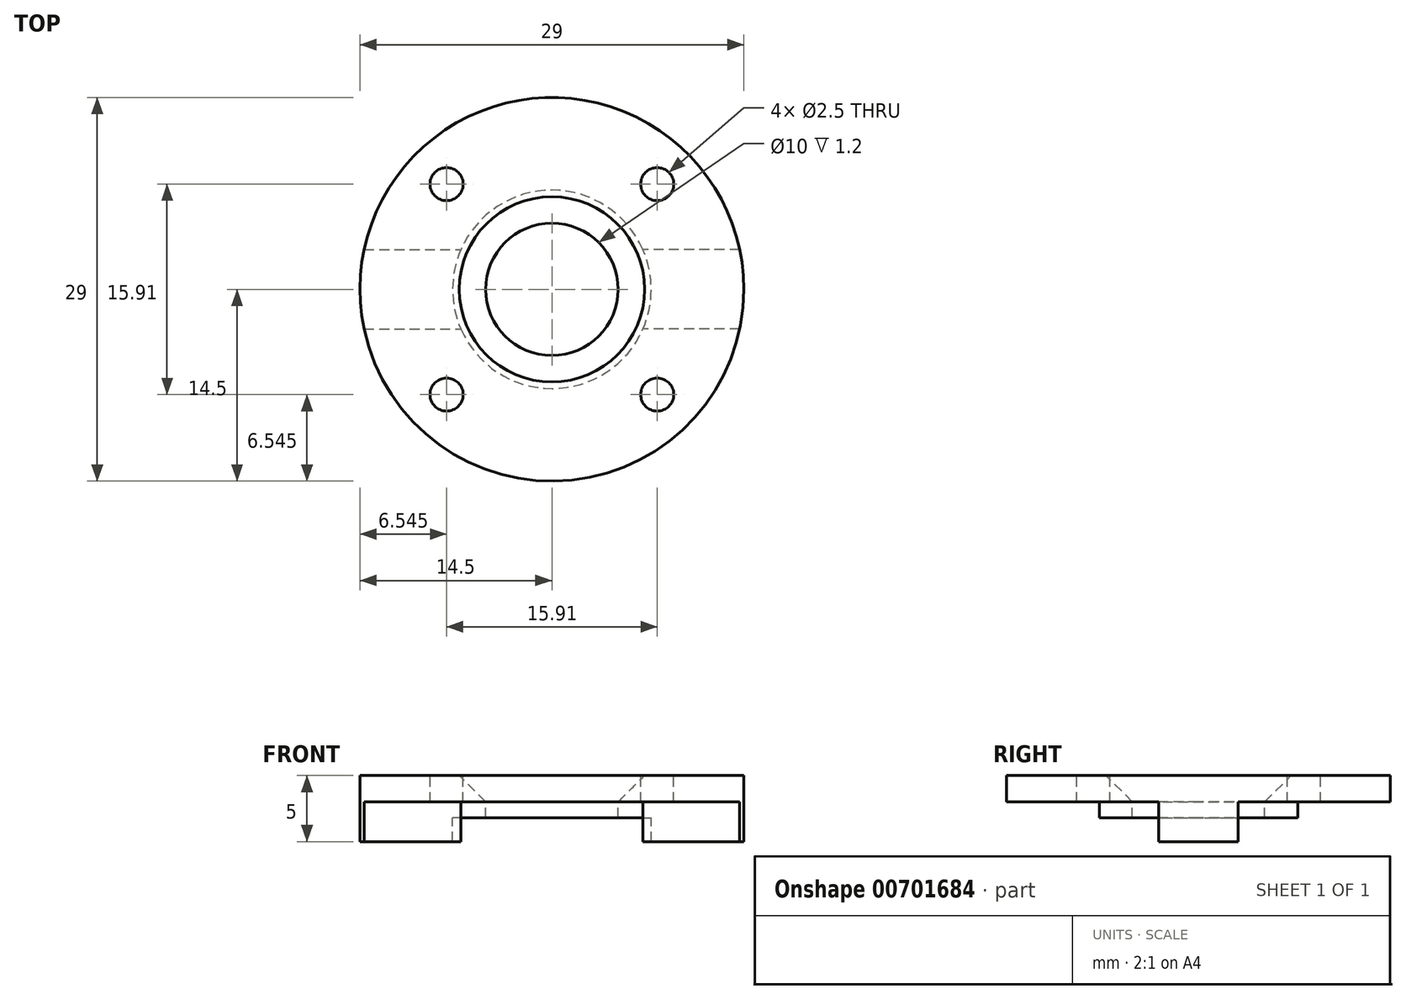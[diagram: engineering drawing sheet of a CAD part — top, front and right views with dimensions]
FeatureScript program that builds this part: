
annotation { "Feature Type Name" : "Feature", "Feature Type Description" : "" }
export const myFeature = defineFeature(function(context is Context, id is Id, definition is map)
    precondition{}
    {
        {
            var Q0;
            Q0=qCreatedBy(makeId("Top.planeOp"),FACE);
            var sketch = newSketch(context, id + "F0", { "sketchPlane" : qUnion([Q0])});
            skCircle(sketch, "E0", {"center": v(0, 0) * mm, "radius": 14.5 * mm});
            skCircle(sketch, "E1", {"center": v(0, 0) * mm, "radius": 5 * mm});
            skCircle(sketch, "E2", {"center": v(0, 0) * mm, "radius": 7.5 * mm});
            skLineSegment(sketch, "E3", {"start": v(-14.19, 3) * mm, "end": v(-6.87, 3) * mm});
            skLineSegment(sketch, "E4.MirrorCS", {"start": v(-14.19, -3) * mm, "end": v(-6.87, -3) * mm});
            skLineSegment(sketch, "E5.MirrorCS", {"start": v(14.19, 3) * mm, "end": v(6.87, 3) * mm});
            skLineSegment(sketch, "E6.MirrorCS", {"start": v(14.19, -3) * mm, "end": v(6.87, -3) * mm});
            skLineSegment(sketch, "E7", {"start": v(0, 0) * mm, "end": v(-14.28, 14.28) * mm, "construction": true});
            skCircle(sketch, "E8", {"center": v(-7.95, 7.95) * mm, "radius": 1.25 * mm});
            skCircle(sketch, "E9.MirrorC", {"center": v(-7.95, -7.95) * mm, "radius": 1.25 * mm});
            skCircle(sketch, "E10.MirrorC", {"center": v(7.95, 7.95) * mm, "radius": 1.25 * mm});
            skCircle(sketch, "E11.MirrorC", {"center": v(7.95, -7.95) * mm, "radius": 1.25 * mm});
            skLineSegment(sketch, "E12", {"start": v(0, 0) * mm, "end": v(40.95, 0) * mm, "construction": true});
            skSolve(sketch);
        }
        {
            assignVariable(context, id + "F1", {"name" : "z0", "anyValue" : 2 * mm});
        }
        {
            var Q0;
            Q0=makeQuery(id+"F0.imprint","IMPRINT",FACE,{"disambiguationData":[TD([[makeQuery(id+"F0.imprint","IMPRINT",EDGE,{"derivedFrom":sQuery(id+"F0.wireOp",EDGE,"E1")}),-1.0]])]});
            extrude(context, id + "F2", {"entities" : qUnion([Q0]), "depth" : getVariable(context, 'z0') + 3 * mm - 1.8 * mm, "offsetDistance" : 25 * mm});
        }
        {
            var Q0;
            {var subQ1=sQuery(id+"F0.wireOp",EDGE,"E3");Q0=makeQuery(id+"F0.imprint","IMPRINT",FACE,{"disambiguationData":[TD([[makeQuery(id+"F0.imprint","IMPRINT",EDGE,{"derivedFrom":subQ1}),1.0]])]});}
            var Q1;
            {var subQ0=sQuery(id+"F0.wireOp",EDGE,"E4.MirrorCS");Q1=makeQuery(id+"F0.imprint","IMPRINT",FACE,{"disambiguationData":[TD([[makeQuery(id+"F0.imprint","IMPRINT",EDGE,{"derivedFrom":subQ0}),-1.0]])]});}
            extrude(context, id + "F3", {"entities" : qUnion([Q0, Q1]), "operationType" : NewBodyOperationType.ADD, "depth" : getVariable(context, 'z0'), "offsetDistance" : 25 * mm});
        }
        {
            var Q0;
            {var subQ0=sQuery(id+"F0.wireOp",EDGE,"E3");Q0=makeQuery(id+"F0.imprint","IMPRINT",FACE,{"disambiguationData":[TD([[makeQuery(id+"F0.imprint","IMPRINT",EDGE,{"derivedFrom":subQ0}),-1.0]])]});}
            var Q1;
            {var subQ0=sQuery(id+"F0.wireOp",EDGE,"E5.MirrorCS");Q1=makeQuery(id+"F0.imprint","IMPRINT",FACE,{"disambiguationData":[TD([[makeQuery(id+"F0.imprint","IMPRINT",EDGE,{"derivedFrom":subQ0}),1.0]])]});}
            extrude(context, id + "F4", {"entities" : qUnion([Q0, Q1]), "operationType" : NewBodyOperationType.ADD, "depth" : getVariable(context, 'z0') + 3 * mm, "offsetDistance" : 25 * mm});
        }
        {
            var Q0;
            Q0=makeQuery(id+"F2.opExtrude","CAP_EDGE",EDGE,{"disambiguationData":[OSD([sQuery(id+"F0.wireOp",EDGE,"E1")])],"isStart":true});
            chamfer(context, id + "F5", {"entities" : qUnion([Q0]), "width" : 2 * mm, "tangentPropagation" : true});
        }
        {
            var Q0;
            Q0=makeQuery(id+"F2.opExtrude","SWEPT_BODY",BODY,{"disambiguationData":[OSD([sQuery(id+"F0.wireOp",EDGE,"E1"),sQuery(id+"F0.wireOp",EDGE,"E2")])]});
            var Q1;
            Q1=sQuery(id+"F0.wireOp",EDGE,"E12");
            transform(context, id + "F6", {"entities" : qUnion([Q0]), "transformType" : TransformType.ROTATION, "transformAxis" : qUnion([Q1]), "angle" : 180 * degree, "makeCopy" : false});
        }
    });
